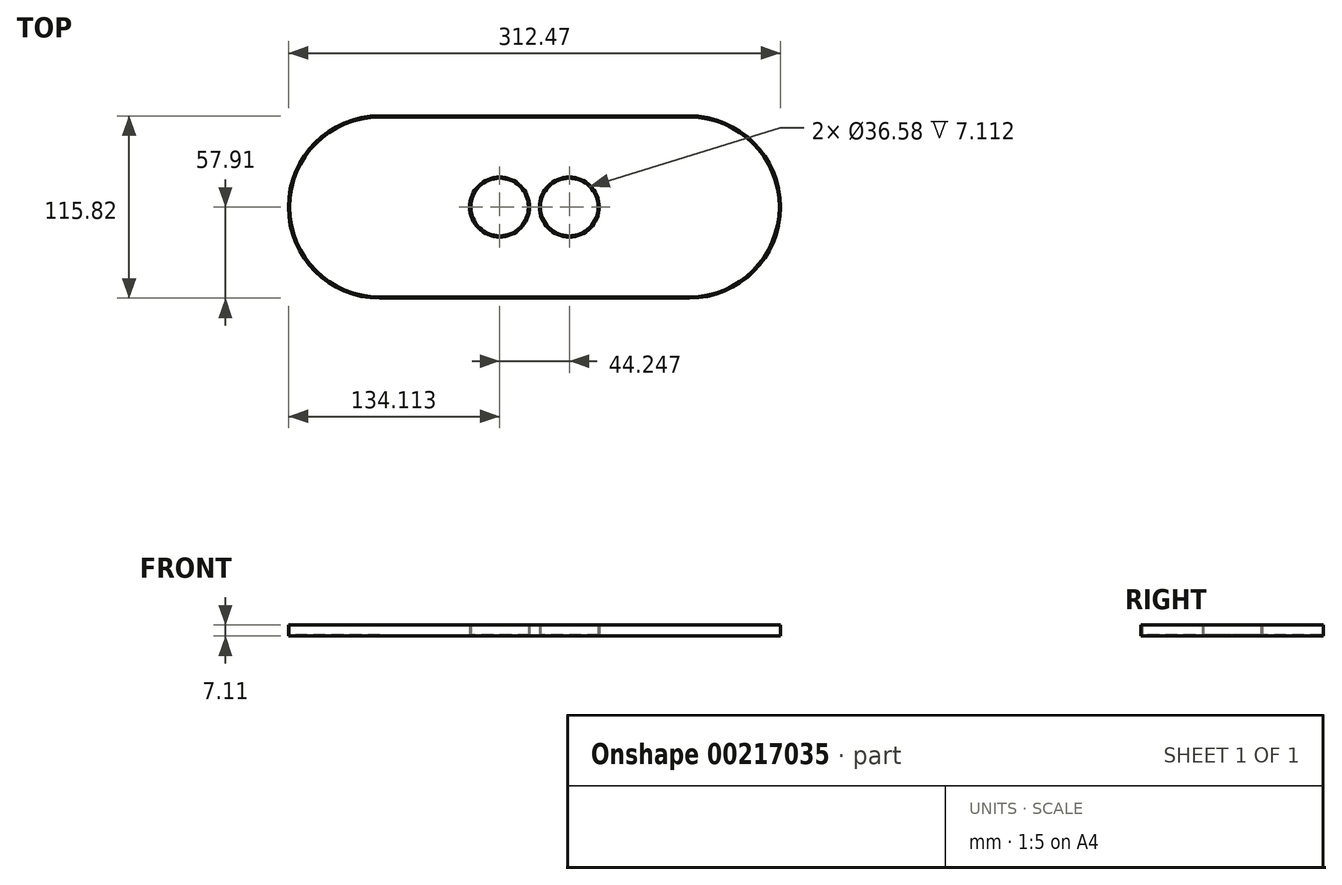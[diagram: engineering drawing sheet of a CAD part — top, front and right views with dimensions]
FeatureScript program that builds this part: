
annotation { "Feature Type Name" : "Feature", "Feature Type Description" : "" }
export const myFeature = defineFeature(function(context is Context, id is Id, definition is map)
    precondition{}
    {
        {
            var Q0;
            Q0=qCreatedBy(makeId("Top.planeOp"),FACE);
            var sketch = newSketch(context, id + "F0", { "sketchPlane" : qUnion([Q0])});
            skCircle(sketch, "E0", {"center": v(-44.25, 0) * mm, "radius": 19.05 * mm});
            skCircle(sketch, "E1", {"center": v(0, 0) * mm, "radius": 19.05 * mm});
            skLineSegment(sketch, "E2", {"start": v(-44.25, -31.75) * mm, "end": v(0, -31.75) * mm});
            skArc(sketch, "E3", {"start": v(-120.45, 57.15) * mm, "mid": v(-177.6, 0) * mm, "end": v(-120.45, -57.15) * mm});
            skArc(sketch, "E4", {"start": v(76.2, -57.15) * mm, "mid": v(133.35, 0) * mm, "end": v(76.2, 57.15) * mm});
            skLineSegment(sketch, "E5", {"start": v(-120.45, 57.15) * mm, "end": v(76.2, 57.15) * mm});
            skLineSegment(sketch, "E6", {"start": v(-120.45, -57.15) * mm, "end": v(76.2, -57.15) * mm});
            skPoint(sketch, "E7.start.orphan", {"position": v(-44.25, 31.75) * mm});
            skPoint(sketch, "E8.orphan", {"position": v(0, 31.75) * mm});
            skSolve(sketch);
        }
        {
            var Q0;
            Q0=makeQuery(id+"F0.imprint","IMPRINT",FACE,{"disambiguationData":[TD([[makeQuery(id+"F0.imprint","IMPRINT",EDGE,{"derivedFrom":sQuery(id+"F0.wireOp",EDGE,"E0")}),-1.0]])]});
            extrude(context, id + "F1", {"entities" : qUnion([Q0]), "depth" : 6.35 * mm});
        }
        {
            var Q0;
            Q0=makeQuery(id+"F1.opExtrude","CAP_FACE",FACE,{"disambiguationData":[OSD([sQuery(id+"F0.wireOp",EDGE,"E0"),sQuery(id+"F0.wireOp",EDGE,"E1"),sQuery(id+"F0.wireOp",EDGE,"9t6qQIlK-74Dw-xPvB-kCsc-Q5Iik9g2cGRT"),sQuery(id+"F0.wireOp",EDGE,"E7"),sQuery(id+"F0.wireOp",EDGE,"E2"),sQuery(id+"F0.wireOp",EDGE,"6de09e63-40c0-455d-9218-0cfe153268a7.trimOffspring")])],"isStart":false});
            shell(context, id + "F2", {"entities" : qUnion([Q0]), "thickness" : 0.76 * mm, "oppositeDirection" : true});
        }
    });
